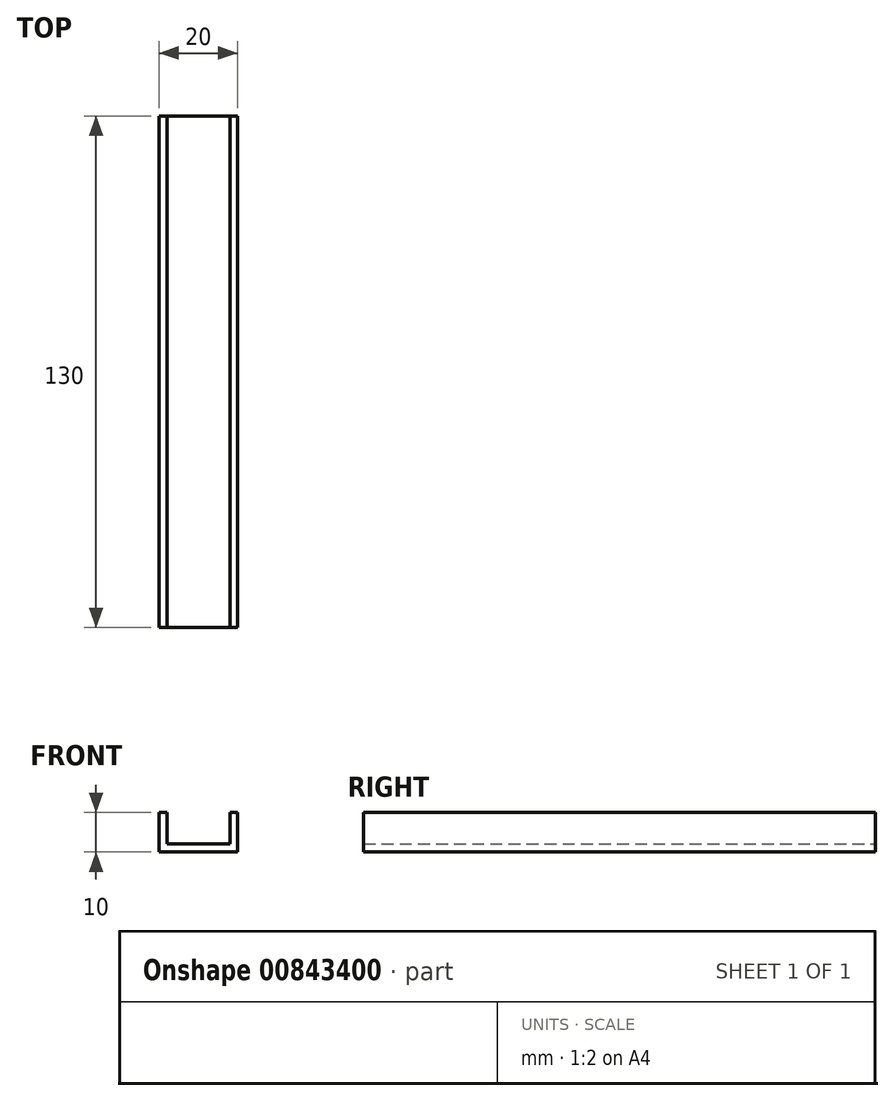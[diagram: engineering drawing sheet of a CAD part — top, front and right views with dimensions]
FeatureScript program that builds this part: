
annotation { "Feature Type Name" : "Feature", "Feature Type Description" : "" }
export const myFeature = defineFeature(function(context is Context, id is Id, definition is map)
    precondition{}
    {
        {
            var Q0;
            Q0=qCreatedBy(makeId("Front.planeOp"),FACE);
            var sketch = newSketch(context, id + "F0", { "sketchPlane" : qUnion([Q0])});
            skLineSegment(sketch, "E0.top", {"start": v(-6.1, -5.3) * mm, "end": v(13.9, -5.3) * mm});
            skLineSegment(sketch, "E0.left", {"start": v(-6.1, 4.7) * mm, "end": v(-6.1, -5.3) * mm});
            skLineSegment(sketch, "E0.right", {"start": v(13.9, 4.7) * mm, "end": v(13.9, -5.3) * mm});
            skPoint(sketch, "E1", {"position": v(13.9, -3.3) * mm});
            skPoint(sketch, "E2", {"position": v(-6.1, -3.3) * mm});
            skLineSegment(sketch, "E3", {"start": v(-4.1, 4.7) * mm, "end": v(-4.1, -5.3) * mm});
            skLineSegment(sketch, "E4", {"start": v(-6.1, -3.3) * mm, "end": v(13.9, -3.3) * mm});
            skLineSegment(sketch, "E5", {"start": v(11.9, 4.7) * mm, "end": v(11.9, -5.3) * mm});
            skPoint(sketch, "E6", {"position": v(-4.1, -3.3) * mm});
            skPoint(sketch, "E7", {"position": v(11.9, -3.3) * mm});
            skPoint(sketch, "E8", {"position": v(-4.1, 4.7) * mm});
            skPoint(sketch, "E9", {"position": v(11.9, 4.7) * mm});
            skPoint(sketch, "E10", {"position": v(13.9, 4.7) * mm});
            skPoint(sketch, "E11", {"position": v(-6.1, 4.7) * mm});
            skPoint(sketch, "E12", {"position": v(-6.1, -5.3) * mm});
            skPoint(sketch, "E13", {"position": v(-4.1, -5.3) * mm});
            skPoint(sketch, "E14", {"position": v(11.9, -5.3) * mm});
            skPoint(sketch, "E15", {"position": v(13.9, -5.3) * mm});
            skLineSegment(sketch, "E16", {"start": v(-6.1, 4.7) * mm, "end": v(-4.1, 4.7) * mm});
            skLineSegment(sketch, "E17", {"start": v(11.9, 4.7) * mm, "end": v(13.9, 4.7) * mm});
            skSolve(sketch);
        }
        {
            var Q0;
            Q0=qSketchRegion(id+"F0",true);
            extrude(context, id + "F1", {"entities" : qUnion([Q0]), "depth" : 130 * mm, "offsetDistance" : 25 * mm});
        }
    });
